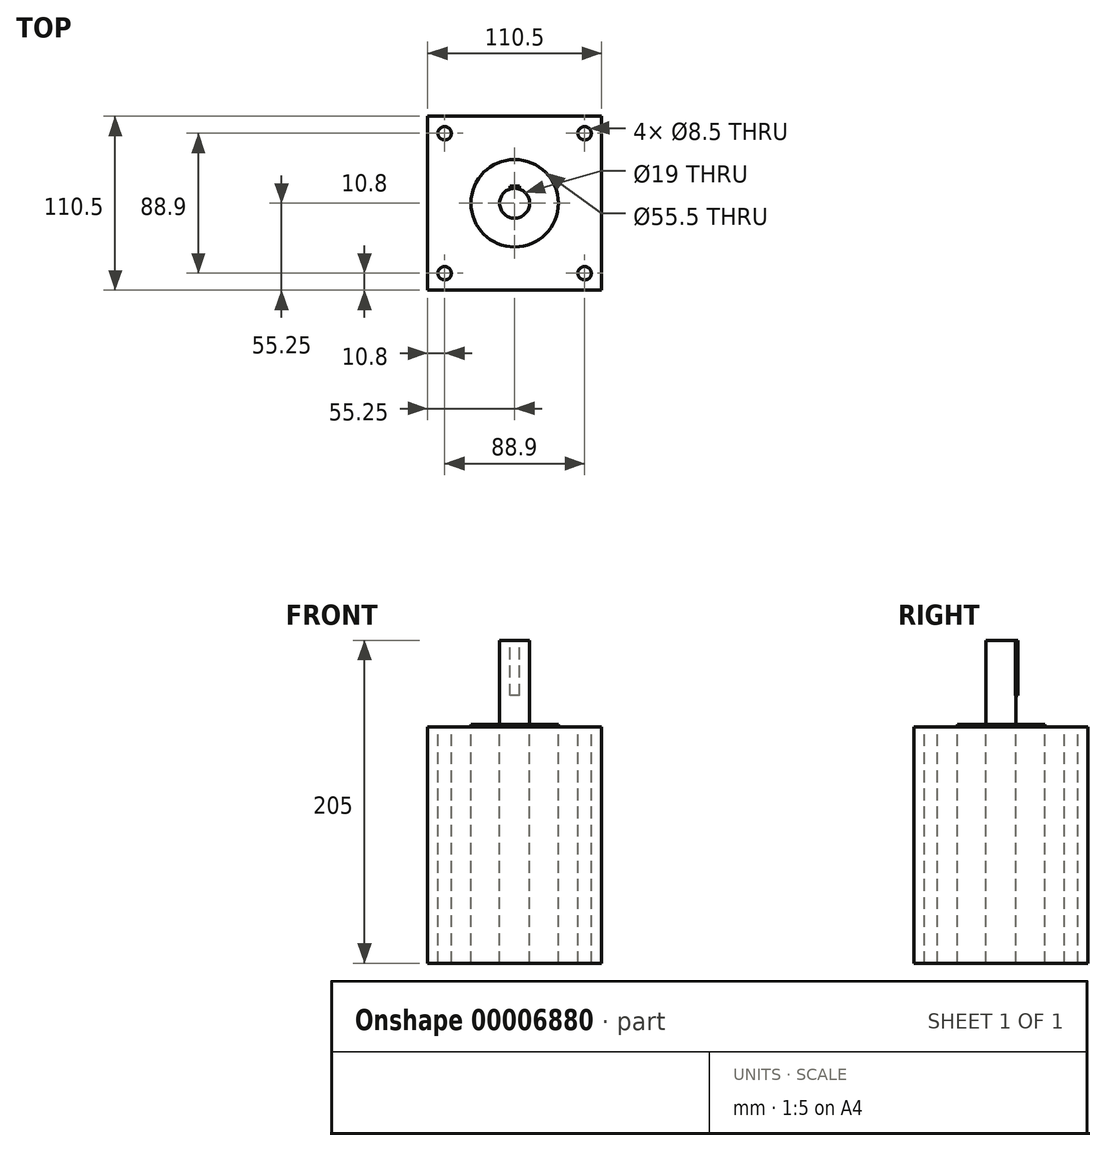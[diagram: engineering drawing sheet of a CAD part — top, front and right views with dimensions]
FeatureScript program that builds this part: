
annotation { "Feature Type Name" : "Feature", "Feature Type Description" : "" }
export const myFeature = defineFeature(function(context is Context, id is Id, definition is map)
    precondition{}
    {
        {
            var Q0;
            Q0=qCreatedBy(makeId("Top.planeOp"),FACE);
            var sketch = newSketch(context, id + "F0", { "sketchPlane" : qUnion([Q0])});
            skLineSegment(sketch, "E0.rect.bottom", {"start": v(55.25, -55.25) * mm, "end": v(-55.25, -55.25) * mm});
            skLineSegment(sketch, "E0.rect.top", {"start": v(55.25, 55.25) * mm, "end": v(-55.25, 55.25) * mm});
            skLineSegment(sketch, "E0.rect.left", {"start": v(55.25, -55.25) * mm, "end": v(55.25, 55.25) * mm});
            skLineSegment(sketch, "E0.rect.right", {"start": v(-55.25, -55.25) * mm, "end": v(-55.25, 55.25) * mm});
            skPoint(sketch, "E0.rect.middle", {"position": v(0, 0) * mm});
            skSolve(sketch);
        }
        {
            var Q0;
            Q0 = qSketchRegion(id + "F0", true);
            extrude(context, id + "F1", {"entities" : qUnion([Q0]), "depth" : 150 * mm});
        }
        {
            var Q0;
            Q0=makeQuery(id+"F1.opExtrude","CAP_FACE",FACE,{"disambiguationData":[OSD([sQuery(id+"F0.wireOp",EDGE,"E0.rect.bottom"),sQuery(id+"F0.wireOp",EDGE,"E0.rect.top"),sQuery(id+"F0.wireOp",EDGE,"E0.rect.left"),sQuery(id+"F0.wireOp",EDGE,"E0.rect.right")])],"isStart":false});
            var sketch = newSketch(context, id + "F2", { "sketchPlane" : qUnion([Q0])});
            skCircle(sketch, "E1", {"center": v(0, 0) * mm, "radius": 27.75 * mm});
            skCircle(sketch, "E2", {"center": v(-44.45, 44.45) * mm, "radius": 4.25 * mm});
            skCircle(sketch, "E3", {"center": v(44.45, 44.45) * mm, "radius": 4.25 * mm});
            skCircle(sketch, "E4", {"center": v(44.45, -44.45) * mm, "radius": 4.25 * mm});
            skCircle(sketch, "E5", {"center": v(-44.45, -44.45) * mm, "radius": 4.25 * mm});
            skCircle(sketch, "E6", {"center": v(0, 0) * mm, "radius": 9.5 * mm});
            skLineSegment(sketch, "E7", {"start": v(-55.25, 0) * mm, "end": v(55.25, 0) * mm, "construction": true});
            skLineSegment(sketch, "E8", {"start": v(0, 55.25) * mm, "end": v(0, -55.25) * mm, "construction": true});
            skSolve(sketch);
        }
        {
            var Q0;
            Q0=makeQuery(id+"F2.imprint","IMPRINT",FACE,{"disambiguationData":[TD([[makeQuery(id+"F2.imprint","IMPRINT",EDGE,{"derivedFrom":sQuery(id+"F2.wireOp",EDGE,"E6")}),1.0]])]});
            extrude(context, id + "F3", {"entities" : qUnion([Q0]), "operationType" : NewBodyOperationType.ADD, "depth" : 55 * mm});
        }
        {
            var Q0;
            Q0=makeQuery(id+"F2.imprint","IMPRINT",FACE,{"disambiguationData":[TD([[makeQuery(id+"F2.imprint","IMPRINT",EDGE,{"derivedFrom":sQuery(id+"F2.wireOp",EDGE,"E1")}),1.0]])]});
            extrude(context, id + "F4", {"entities" : qUnion([Q0]), "operationType" : NewBodyOperationType.ADD, "depth" : 1.6 * mm});
        }
        {
            var Q0;
            Q0=makeQuery(id+"F2.imprint","IMPRINT",FACE,{"disambiguationData":[TD([[makeQuery(id+"F2.imprint","IMPRINT",EDGE,{"derivedFrom":sQuery(id+"F2.wireOp",EDGE,"E3")}),1.0]])]});
            var Q1;
            Q1=makeQuery(id+"F2.imprint","IMPRINT",FACE,{"disambiguationData":[TD([[makeQuery(id+"F2.imprint","IMPRINT",EDGE,{"derivedFrom":sQuery(id+"F2.wireOp",EDGE,"E4")}),1.0]])]});
            var Q2;
            Q2=makeQuery(id+"F2.imprint","IMPRINT",FACE,{"disambiguationData":[TD([[makeQuery(id+"F2.imprint","IMPRINT",EDGE,{"derivedFrom":sQuery(id+"F2.wireOp",EDGE,"E1")}),1.0]])]});
            var Q3;
            Q3=makeQuery(id+"F2.imprint","IMPRINT",FACE,{"disambiguationData":[TD([[makeQuery(id+"F2.imprint","IMPRINT",EDGE,{"derivedFrom":sQuery(id+"F2.wireOp",EDGE,"E2")}),1.0]])]});
            var Q4;
            Q4=makeQuery(id+"F2.imprint","IMPRINT",FACE,{"disambiguationData":[TD([[makeQuery(id+"F2.imprint","IMPRINT",EDGE,{"derivedFrom":sQuery(id+"F2.wireOp",EDGE,"E5")}),1.0]])]});
            extrude(context, id + "F5", {"entities" : qUnion([Q0, Q1, Q2, Q3, Q4]), "operationType" : NewBodyOperationType.REMOVE, "endBound" : BoundingType.THROUGH_ALL, "oppositeDirection" : true, "depth" : 25 * mm});
        }
        {
            var Q0;
            Q0=makeQuery(id+"F3.opExtrude","CAP_FACE",FACE,{"disambiguationData":[OSD([sQuery(id+"F2.wireOp",EDGE,"E6")])],"isStart":false});
            var sketch = newSketch(context, id + "F6", { "sketchPlane" : qUnion([Q0])});
            skLineSegment(sketch, "E9", {"start": v(0, 0) * mm, "end": v(0, 9.5) * mm, "construction": true});
            skLineSegment(sketch, "E10", {"start": v(0, 9.5) * mm, "end": v(0, -9.5) * mm, "construction": true});
            skLineSegment(sketch, "E11", {"start": v(-9.5, 0) * mm, "end": v(9.5, 0) * mm, "construction": true});
            skLineSegment(sketch, "E12.rect.top", {"start": v(3, 10.83) * mm, "end": v(-3, 10.83) * mm});
            skLineSegment(sketch, "E12.rect.left", {"start": v(3, 9.01) * mm, "end": v(3, 10.83) * mm});
            skLineSegment(sketch, "E12.rect.right", {"start": v(-3, 9.01) * mm, "end": v(-3, 10.83) * mm});
            skPoint(sketch, "E12.rect.middle", {"position": v(0, 9.5) * mm});
            skCircle(sketch, "E13", {"center": v(0, 0) * mm, "radius": 9.5 * mm});
            skPoint(sketch, "E14.orphan", {"position": v(3, 8.17) * mm});
            skPoint(sketch, "E15.orphan", {"position": v(-3, 8.17) * mm});
            skSolve(sketch);
        }
        {
            var Q0;
            Q0=makeQuery(id+"F6.imprint","IMPRINT",FACE,{"disambiguationData":[TD([[makeQuery(id+"F6.imprint","IMPRINT",EDGE,{"derivedFrom":sQuery(id+"F6.wireOp",EDGE,"E12.rect.top")}),1.0]])]});
            extrude(context, id + "F7", {"entities" : qUnion([Q0]), "oppositeDirection" : true, "depth" : 35 * mm});
        }
        {
            var Q0;
            Q0=makeQuery(id+"F5.boolean.opBoolean","COPY",FACE,{"derivedFrom":makeQuery(id+"F5.opExtrude","CAP_FACE",FACE,{"disambiguationData":[OSD([sQuery(id+"F2.wireOp",EDGE,"E1"),sQuery(id+"F2.wireOp",EDGE,"E6")])],"isStart":true})});
            extrude(context, id + "F8", {"entities" : qUnion([Q0]), "depth" : (150) * mm});
        }
    });
